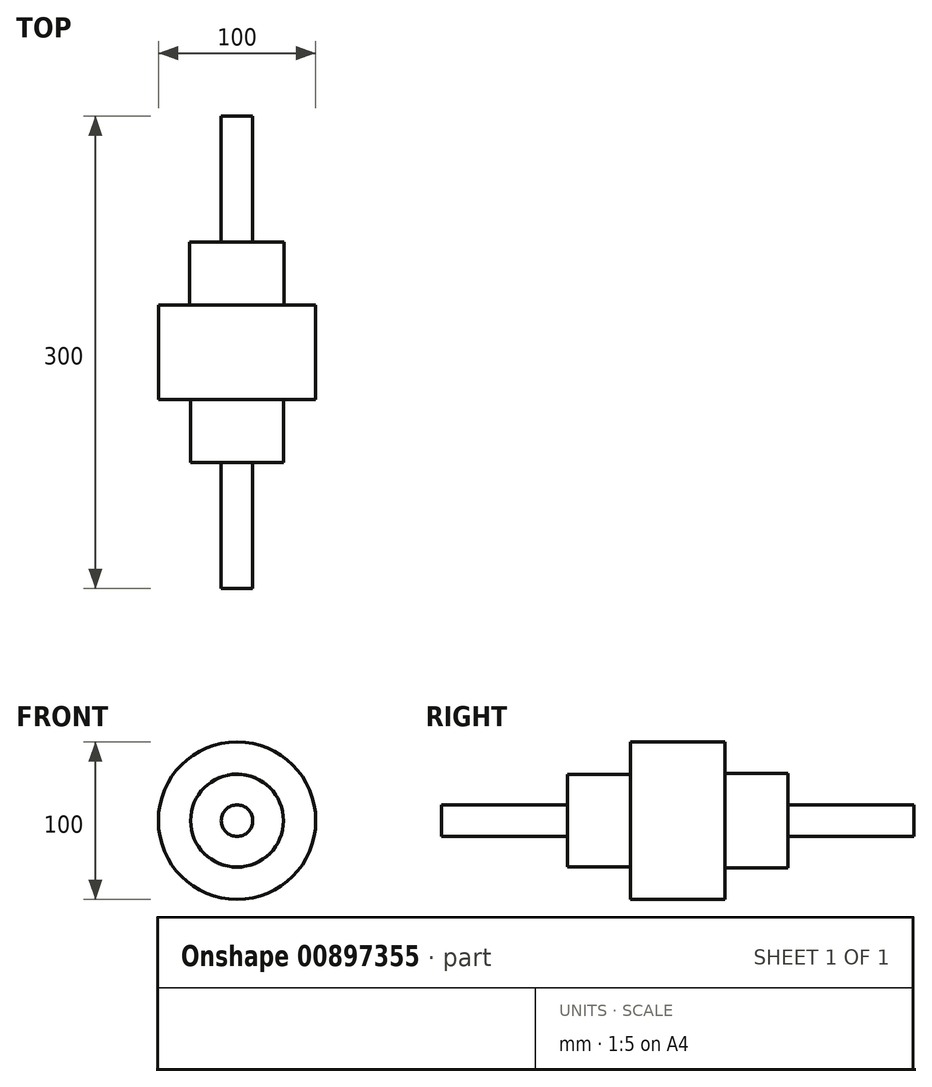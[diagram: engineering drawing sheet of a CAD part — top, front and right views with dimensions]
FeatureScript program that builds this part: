
annotation { "Feature Type Name" : "Feature", "Feature Type Description" : "" }
export const myFeature = defineFeature(function(context is Context, id is Id, definition is map)
    precondition{}
    {
        {
            var Q0;
            Q0=qCreatedBy(makeId("Front.planeOp"),FACE);
            var sketch = newSketch(context, id + "F0", { "sketchPlane" : qUnion([Q0])});
            skCircle(sketch, "E0", {"center": v(0, 0) * mm, "radius": 50 * mm});
            skSolve(sketch);
        }
        {
            var Q0;
            Q0=makeQuery(id+"F0.imprint","IMPRINT",FACE,{"disambiguationData":[TD([[makeQuery(id+"F0.imprint","IMPRINT",EDGE,{"derivedFrom":sQuery(id+"F0.wireOp",EDGE,"E0")}),1.0]])]});
            extrude(context, id + "F1", {"entities" : qUnion([Q0]), "depth" : 60 * mm, "offsetDistance" : 25.4 * mm});
        }
        {
            var Q0;
            Q0=qCreatedBy(makeId("Front.planeOp"),FACE);
            var sketch = newSketch(context, id + "F2", { "sketchPlane" : qUnion([Q0])});
            skCircle(sketch, "E1", {"center": v(0, 0) * mm, "radius": 30 * mm});
            skSolve(sketch);
        }
        {
            var Q0;
            Q0=makeQuery(id+"F2.imprint","IMPRINT",FACE,{"disambiguationData":[TD([[makeQuery(id+"F2.imprint","IMPRINT",EDGE,{"derivedFrom":sQuery(id+"F2.wireOp",EDGE,"E1")}),1.0]])]});
            extrude(context, id + "F3", {"entities" : qUnion([Q0]), "operationType" : NewBodyOperationType.ADD, "oppositeDirection" : true, "depth" : 40 * mm, "offsetDistance" : 25.4 * mm});
        }
        {
            var Q0;
            Q0=makeQuery(id+"F3.opExtrude","CAP_FACE",FACE,{"disambiguationData":[OSD([sQuery(id+"F2.wireOp",EDGE,"E1")])],"isStart":false});
            var sketch = newSketch(context, id + "F4", { "sketchPlane" : qUnion([Q0])});
            skCircle(sketch, "E2", {"center": v(0, 0) * mm, "radius": 10 * mm});
            skSolve(sketch);
        }
        {
            var Q0;
            Q0=makeQuery(id+"F4.imprint","IMPRINT",FACE,{"disambiguationData":[TD([[makeQuery(id+"F4.imprint","IMPRINT",EDGE,{"derivedFrom":sQuery(id+"F4.wireOp",EDGE,"E2")}),1.0]])]});
            extrude(context, id + "F5", {"entities" : qUnion([Q0]), "operationType" : NewBodyOperationType.ADD, "depth" : 80 * mm, "offsetDistance" : 25.4 * mm});
        }
        {
            var Q0;
            Q0=makeQuery(id+"F1.opExtrude","CAP_FACE",FACE,{"disambiguationData":[OSD([sQuery(id+"F0.wireOp",EDGE,"E0")])],"isStart":false});
            var sketch = newSketch(context, id + "F6", { "sketchPlane" : qUnion([Q0])});
            skCircle(sketch, "E3", {"center": v(0, 0) * mm, "radius": 29.46 * mm});
            skSolve(sketch);
        }
        {
            var Q0;
            Q0=makeQuery(id+"F6.imprint","IMPRINT",FACE,{"disambiguationData":[TD([[makeQuery(id+"F6.imprint","IMPRINT",EDGE,{"derivedFrom":sQuery(id+"F6.wireOp",EDGE,"E3")}),1.0]])]});
            extrude(context, id + "F7", {"entities" : qUnion([Q0]), "operationType" : NewBodyOperationType.ADD, "depth" : 40 * mm, "offsetDistance" : 25.4 * mm});
        }
        {
            var Q0;
            Q0=makeQuery(id+"F7.opExtrude","CAP_FACE",FACE,{"disambiguationData":[OSD([sQuery(id+"F6.wireOp",EDGE,"E3")])],"isStart":false});
            var sketch = newSketch(context, id + "F8", { "sketchPlane" : qUnion([Q0])});
            skCircle(sketch, "E4", {"center": v(0, 0) * mm, "radius": 10 * mm});
            skSolve(sketch);
        }
        {
            var Q0;
            Q0=makeQuery(id+"F8.imprint","IMPRINT",FACE,{"disambiguationData":[TD([[makeQuery(id+"F8.imprint","IMPRINT",EDGE,{"derivedFrom":sQuery(id+"F8.wireOp",EDGE,"E4")}),1.0]])]});
            extrude(context, id + "F9", {"entities" : qUnion([Q0]), "operationType" : NewBodyOperationType.ADD, "depth" : 80 * mm, "offsetDistance" : 25.4 * mm});
        }
    });
